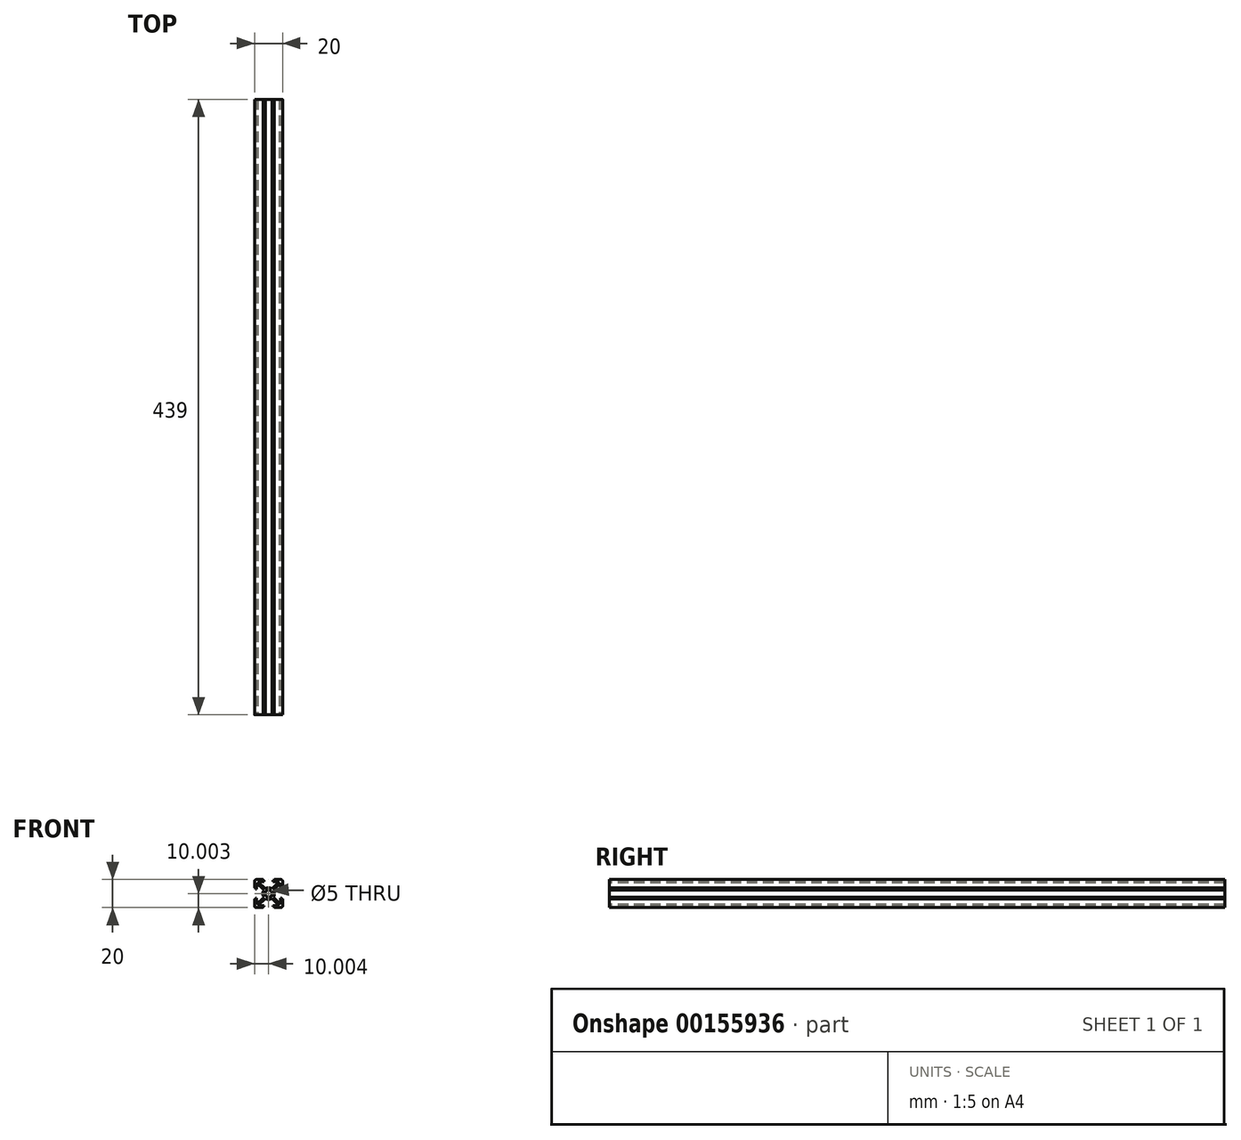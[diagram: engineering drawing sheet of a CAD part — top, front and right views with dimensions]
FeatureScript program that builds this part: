
annotation { "Feature Type Name" : "Feature", "Feature Type Description" : "" }
export const myFeature = defineFeature(function(context is Context, id is Id, definition is map)
    precondition{}
    {
        {
            var Q0;
            Q0=qCreatedBy(makeId("Front.planeOp"),FACE);
            var sketch = newSketch(context, id + "F0", { "sketchPlane" : qUnion([Q0])});
            skArc(sketch, "E0", {"start": v(-44.98, 42.64) * mm, "mid": v(-45.76, 40.2) * mm, "end": v(-44.98, 37.77) * mm});
            skCircle(sketch, "E1", {"center": v(-41.56, 40.2) * mm, "radius": 2.5 * mm});
            skLineSegment(sketch, "E2", {"start": v(-54.61, 53.26) * mm, "end": v(-41.56, 40.2) * mm, "construction": true});
            skLineSegment(sketch, "E3", {"start": v(-41.56, 40.2) * mm, "end": v(-28.67, 27.32) * mm, "construction": true});
            skLineSegment(sketch, "E4", {"start": v(-41.56, 40.2) * mm, "end": v(-29.82, 51.94) * mm, "construction": true});
            skLineSegment(sketch, "E5", {"start": v(-41.56, 40.2) * mm, "end": v(-53.14, 28.61) * mm, "construction": true});
            skLineSegment(sketch, "E6", {"start": v(-55.54, 40.2) * mm, "end": v(-21.72, 40.2) * mm, "construction": true});
            skLineSegment(sketch, "E7", {"start": v(-41.56, 50.17) * mm, "end": v(-41.56, 24.27) * mm, "construction": true});
            skLineSegment(sketch, "E8", {"start": v(-50.36, 50.2) * mm, "end": v(-45.5, 50.2) * mm});
            skLineSegment(sketch, "E9", {"start": v(-44.76, 49.6) * mm, "end": v(-44.76, 48.8) * mm});
            skLineSegment(sketch, "E10", {"start": v(-49.17, 48.8) * mm, "end": v(-43.99, 43.63) * mm});
            skLineSegment(sketch, "E11", {"start": v(-44.76, 48.8) * mm, "end": v(-49.17, 48.8) * mm});
            skLineSegment(sketch, "E12", {"start": v(-45.5, 50.2) * mm, "end": v(-45.5, 49.6) * mm});
            skLineSegment(sketch, "E13", {"start": v(-45.5, 49.6) * mm, "end": v(-44.76, 49.6) * mm});
            skPoint(sketch, "E14.orphan", {"position": v(-44.76, 50.2) * mm});
            skLineSegment(sketch, "E15.MirrorCS", {"start": v(-50.16, 47.81) * mm, "end": v(-44.98, 42.64) * mm});
            skLineSegment(sketch, "E16.MirrorCS", {"start": v(-50.16, 43.4) * mm, "end": v(-50.16, 47.81) * mm});
            skLineSegment(sketch, "E17.MirrorCS", {"start": v(-50.95, 43.4) * mm, "end": v(-50.16, 43.4) * mm});
            skLineSegment(sketch, "E18.MirrorCS", {"start": v(-50.95, 44.15) * mm, "end": v(-50.95, 43.4) * mm});
            skLineSegment(sketch, "E19.MirrorCS", {"start": v(-51.56, 49) * mm, "end": v(-51.56, 44.15) * mm});
            skLineSegment(sketch, "E20.MirrorCS", {"start": v(-51.56, 44.15) * mm, "end": v(-50.95, 44.15) * mm});
            skLineSegment(sketch, "E21.MirrorCS", {"start": v(-32.96, 47.81) * mm, "end": v(-38.13, 42.64) * mm});
            skLineSegment(sketch, "E22.MirrorCS", {"start": v(-33.95, 48.8) * mm, "end": v(-39.12, 43.63) * mm});
            skLineSegment(sketch, "E23.MirrorCS", {"start": v(-37.6, 49.6) * mm, "end": v(-38.36, 49.6) * mm});
            skLineSegment(sketch, "E24.MirrorCS", {"start": v(-32.16, 44.15) * mm, "end": v(-32.16, 43.4) * mm});
            skLineSegment(sketch, "E25.MirrorCS", {"start": v(-31.56, 44.15) * mm, "end": v(-32.16, 44.15) * mm});
            skLineSegment(sketch, "E26.MirrorCS", {"start": v(-38.36, 49.6) * mm, "end": v(-38.36, 48.8) * mm});
            skLineSegment(sketch, "E27.MirrorCS", {"start": v(-37.6, 50.2) * mm, "end": v(-37.6, 49.6) * mm});
            skLineSegment(sketch, "E28.MirrorCS", {"start": v(-32.16, 43.4) * mm, "end": v(-32.96, 43.4) * mm});
            skLineSegment(sketch, "E29.MirrorCS", {"start": v(-32.96, 43.4) * mm, "end": v(-32.96, 47.81) * mm});
            skPoint(sketch, "E30.MirrorP", {"position": v(-38.36, 50.2) * mm});
            skLineSegment(sketch, "E31.MirrorCS", {"start": v(-38.36, 48.8) * mm, "end": v(-33.95, 48.8) * mm});
            skLineSegment(sketch, "E32.MirrorCS", {"start": v(-32.76, 50.2) * mm, "end": v(-37.6, 50.2) * mm});
            skLineSegment(sketch, "E33.MirrorCS", {"start": v(-31.56, 49) * mm, "end": v(-31.56, 44.15) * mm});
            skLineSegment(sketch, "E34.MirrorCS", {"start": v(-32.16, 37) * mm, "end": v(-32.96, 37) * mm});
            skLineSegment(sketch, "E35.MirrorCS", {"start": v(-38.36, 30.8) * mm, "end": v(-38.36, 31.6) * mm});
            skLineSegment(sketch, "E36.MirrorCS", {"start": v(-32.16, 36.25) * mm, "end": v(-32.16, 37) * mm});
            skLineSegment(sketch, "E37.MirrorCS", {"start": v(-37.6, 30.8) * mm, "end": v(-38.36, 30.8) * mm});
            skLineSegment(sketch, "E38.MirrorCS", {"start": v(-31.56, 36.25) * mm, "end": v(-32.16, 36.25) * mm});
            skLineSegment(sketch, "E39.MirrorCS", {"start": v(-37.6, 30.2) * mm, "end": v(-37.6, 30.8) * mm});
            skLineSegment(sketch, "E40.MirrorCS", {"start": v(-32.76, 30.2) * mm, "end": v(-37.6, 30.2) * mm});
            skLineSegment(sketch, "E41.MirrorCS", {"start": v(-31.56, 31.4) * mm, "end": v(-31.56, 36.25) * mm});
            skLineSegment(sketch, "E42.MirrorCS", {"start": v(-33.95, 31.6) * mm, "end": v(-39.12, 36.78) * mm});
            skLineSegment(sketch, "E43.MirrorCS", {"start": v(-32.96, 37) * mm, "end": v(-32.96, 32.6) * mm});
            skPoint(sketch, "E44.MirrorP", {"position": v(-38.36, 30.2) * mm});
            skLineSegment(sketch, "E45.MirrorCS", {"start": v(-38.36, 31.6) * mm, "end": v(-33.95, 31.6) * mm});
            skLineSegment(sketch, "E46.MirrorCS", {"start": v(-32.96, 32.6) * mm, "end": v(-38.13, 37.77) * mm});
            skLineSegment(sketch, "E47.MirrorCS", {"start": v(-45.5, 30.8) * mm, "end": v(-44.76, 30.8) * mm});
            skLineSegment(sketch, "E48.MirrorCS", {"start": v(-51.56, 36.25) * mm, "end": v(-50.95, 36.25) * mm});
            skLineSegment(sketch, "E49.MirrorCS", {"start": v(-50.95, 36.25) * mm, "end": v(-50.95, 37) * mm});
            skLineSegment(sketch, "E50.MirrorCS", {"start": v(-50.95, 37) * mm, "end": v(-50.16, 37) * mm});
            skLineSegment(sketch, "E51.MirrorCS", {"start": v(-45.5, 30.2) * mm, "end": v(-45.5, 30.8) * mm});
            skLineSegment(sketch, "E52.MirrorCS", {"start": v(-44.76, 30.8) * mm, "end": v(-44.76, 31.6) * mm});
            skLineSegment(sketch, "E53.MirrorCS", {"start": v(-50.16, 37) * mm, "end": v(-50.16, 32.6) * mm});
            skLineSegment(sketch, "E54.MirrorCS", {"start": v(-50.16, 32.6) * mm, "end": v(-44.98, 37.77) * mm});
            skLineSegment(sketch, "E55.MirrorCS", {"start": v(-50.36, 30.2) * mm, "end": v(-45.5, 30.2) * mm});
            skPoint(sketch, "E56.MirrorP", {"position": v(-44.76, 30.2) * mm});
            skLineSegment(sketch, "E57.MirrorCS", {"start": v(-51.56, 31.4) * mm, "end": v(-51.56, 36.25) * mm});
            skLineSegment(sketch, "E58.MirrorCS", {"start": v(-49.17, 31.6) * mm, "end": v(-43.99, 36.78) * mm});
            skLineSegment(sketch, "E59.MirrorCS", {"start": v(-44.76, 31.6) * mm, "end": v(-49.17, 31.6) * mm});
            skPoint(sketch, "E60.visualSharp", {"position": v(-51.56, 50.2) * mm});
            skArc(sketch, "E60.filletArc", {"start": v(-50.36, 50.2) * mm, "mid": v(-51.2, 49.85) * mm, "end": v(-51.56, 49) * mm});
            skPoint(sketch, "E61.visualSharp", {"position": v(-31.56, 50.2) * mm});
            skArc(sketch, "E61.filletArc", {"start": v(-31.56, 49) * mm, "mid": v(-31.9, 49.85) * mm, "end": v(-32.76, 50.2) * mm});
            skPoint(sketch, "E62.visualSharp", {"position": v(-31.56, 30.2) * mm});
            skArc(sketch, "E62.filletArc", {"start": v(-32.76, 30.2) * mm, "mid": v(-31.9, 30.55) * mm, "end": v(-31.56, 31.4) * mm});
            skPoint(sketch, "E63.visualSharp", {"position": v(-51.56, 30.2) * mm});
            skArc(sketch, "E63.filletArc", {"start": v(-51.56, 31.4) * mm, "mid": v(-51.2, 30.55) * mm, "end": v(-50.36, 30.2) * mm});
            skArc(sketch, "E64.trimOffspring", {"start": v(-39.12, 43.63) * mm, "mid": v(-41.56, 44.4) * mm, "end": v(-43.99, 43.63) * mm});
            skArc(sketch, "E65.trimOffspring", {"start": v(-43.99, 36.78) * mm, "mid": v(-41.56, 36) * mm, "end": v(-39.12, 36.78) * mm});
            skArc(sketch, "E66.trimOffspring", {"start": v(-38.13, 37.77) * mm, "mid": v(-37.36, 40.2) * mm, "end": v(-38.13, 42.64) * mm});
            skSolve(sketch);
        }
        {
            var Q0;
            Q0=makeQuery(id+"F0.imprint","IMPRINT",FACE,{"disambiguationData":[TD([[makeQuery(id+"F0.imprint","IMPRINT",EDGE,{"derivedFrom":sQuery(id+"F0.wireOp",EDGE,"E0")}),1.0]])]});
            extrude(context, id + "F1", {"entities" : qUnion([Q0]), "oppositeDirection" : true, "depth" : 439 * mm, "offsetDistance" : 25 * mm});
        }
    });
